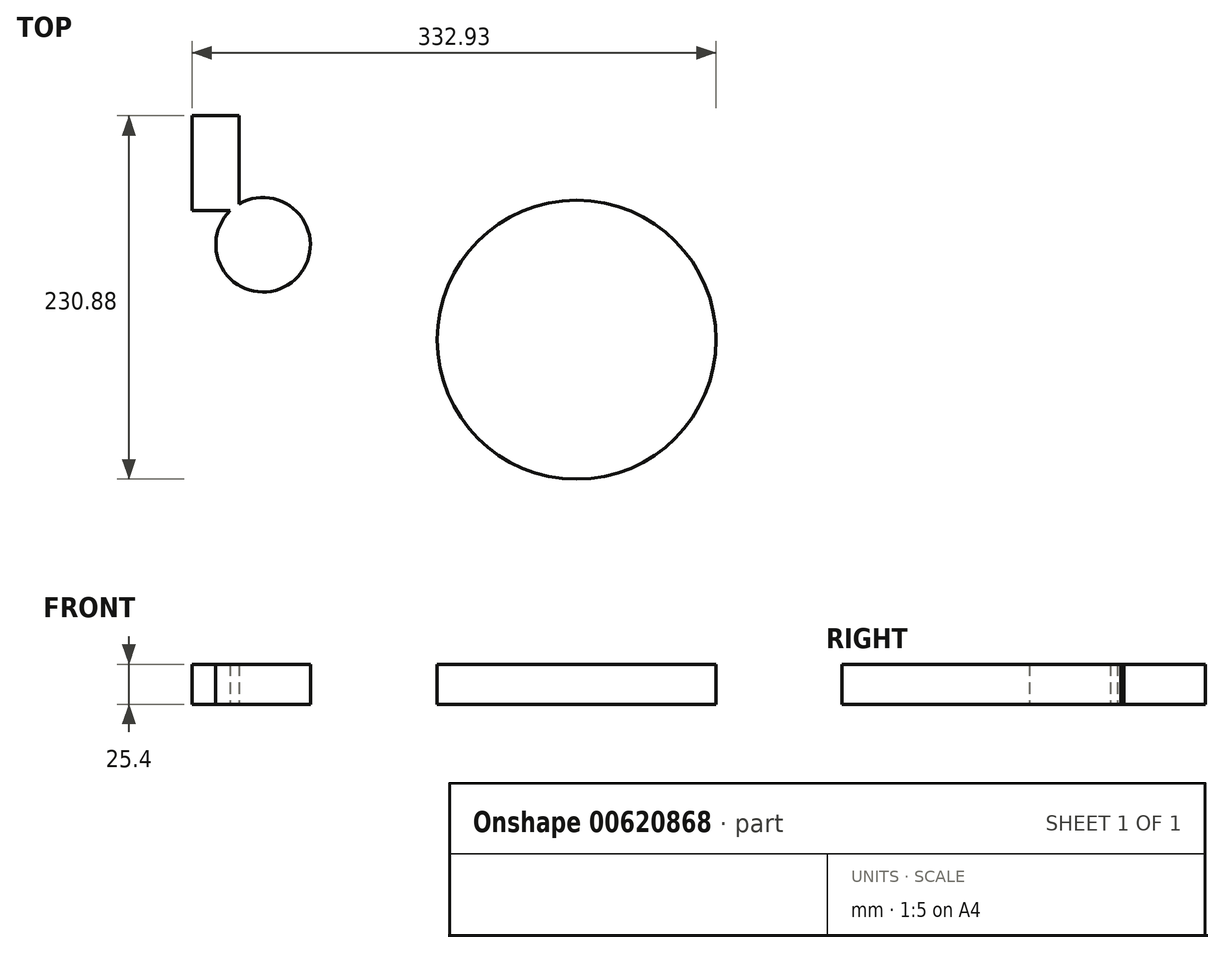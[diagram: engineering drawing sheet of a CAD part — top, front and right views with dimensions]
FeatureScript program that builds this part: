
annotation { "Feature Type Name" : "Feature", "Feature Type Description" : "" }
export const myFeature = defineFeature(function(context is Context, id is Id, definition is map)
    precondition{}
    {
        {
            var Q0;
            Q0=qCreatedBy(makeId("Top.planeOp"),FACE);
            var sketch = newSketch(context, id + "F0", { "sketchPlane" : qUnion([Q0])});
            skLineSegment(sketch, "E0.bottom", {"start": v(0, 0) * mm, "end": v(-30.1, 0) * mm});
            skLineSegment(sketch, "E0.top", {"start": v(0, 60.33) * mm, "end": v(-30.1, 60.33) * mm});
            skLineSegment(sketch, "E0.left", {"start": v(0, 0) * mm, "end": v(0, 60.33) * mm});
            skLineSegment(sketch, "E0.right", {"start": v(-30.1, 0) * mm, "end": v(-30.1, 60.33) * mm});
            skCircle(sketch, "E1", {"center": v(15.13, -21.62) * mm, "radius": 30.02 * mm});
            skCircle(sketch, "E2", {"center": v(214.25, -81.97) * mm, "radius": 88.58 * mm});
            skSolve(sketch);
        }
        {
            var Q0;
            Q0 = qSketchRegion(id + "Fj5agJSak7sPJLT_0", true);
            var Q1;
            Q1 = qSketchRegion(id + "F0", true);
            extrude(context, id + "F1", {"entities" : qUnion([Q0, Q1]), "depth" : 25.4 * mm, "offsetDistance" : 25.4 * mm});
        }
    });
